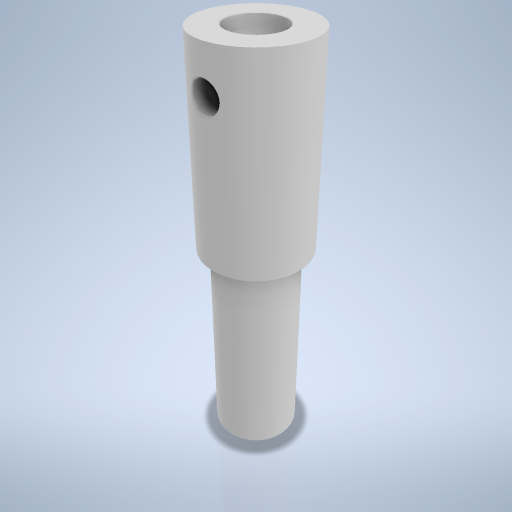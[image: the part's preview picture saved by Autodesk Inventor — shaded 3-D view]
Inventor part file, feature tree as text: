
AUTODESK INVENTOR PART (.ipt)
format: ipt  version: 2024.2 (Build 282272000, 272)  size: 274,432 bytes
history: native  units: mm
features: sketch x3, revolve x1, plane x1, hole x1, extrude x1, chamfer x1
ambient origin geometry x8: Origin, YZ Plane, XZ Plane, XY Plane, X Axis, Y Axis, Z Axis, Center Point
bodies: Volumenkörper1 (feature_tree)
feature tree (8):
  revolve  "Umdrehung1"
  plane  "Arbeitsebene1"
  hole  "Bohrung1"  [1 undecoded]
  extrude  "Extrusion1"  Depth=28.0mm
  chamfer  "Fasen1"  Distance=18.0mm
  sketch  "Skizze1"  dims[d0=74.0mm d1=66.0mm]
  sketch  "Skizze2"  dims[d5=36.0mm d6=28.0mm]
  sketch  "Skizze3"  dims[d7=90.0deg d8=18.0mm d9=14.0mm d10=10.0mm d11=6.0mm d12=4.0mm d13=2.0mm d14=90.0deg d15=8.0mm d16=20.594885mm d17=18.0mm d18=90.0mm d19=0.0mm d20=2.0mm d21=2.0mm d22=45.0deg]
note: 1 required parameter value undecoded (feature->parameter linkage not recoverable at this tier; creation-order binding heuristic only, values carry confidence <= 0.55)
